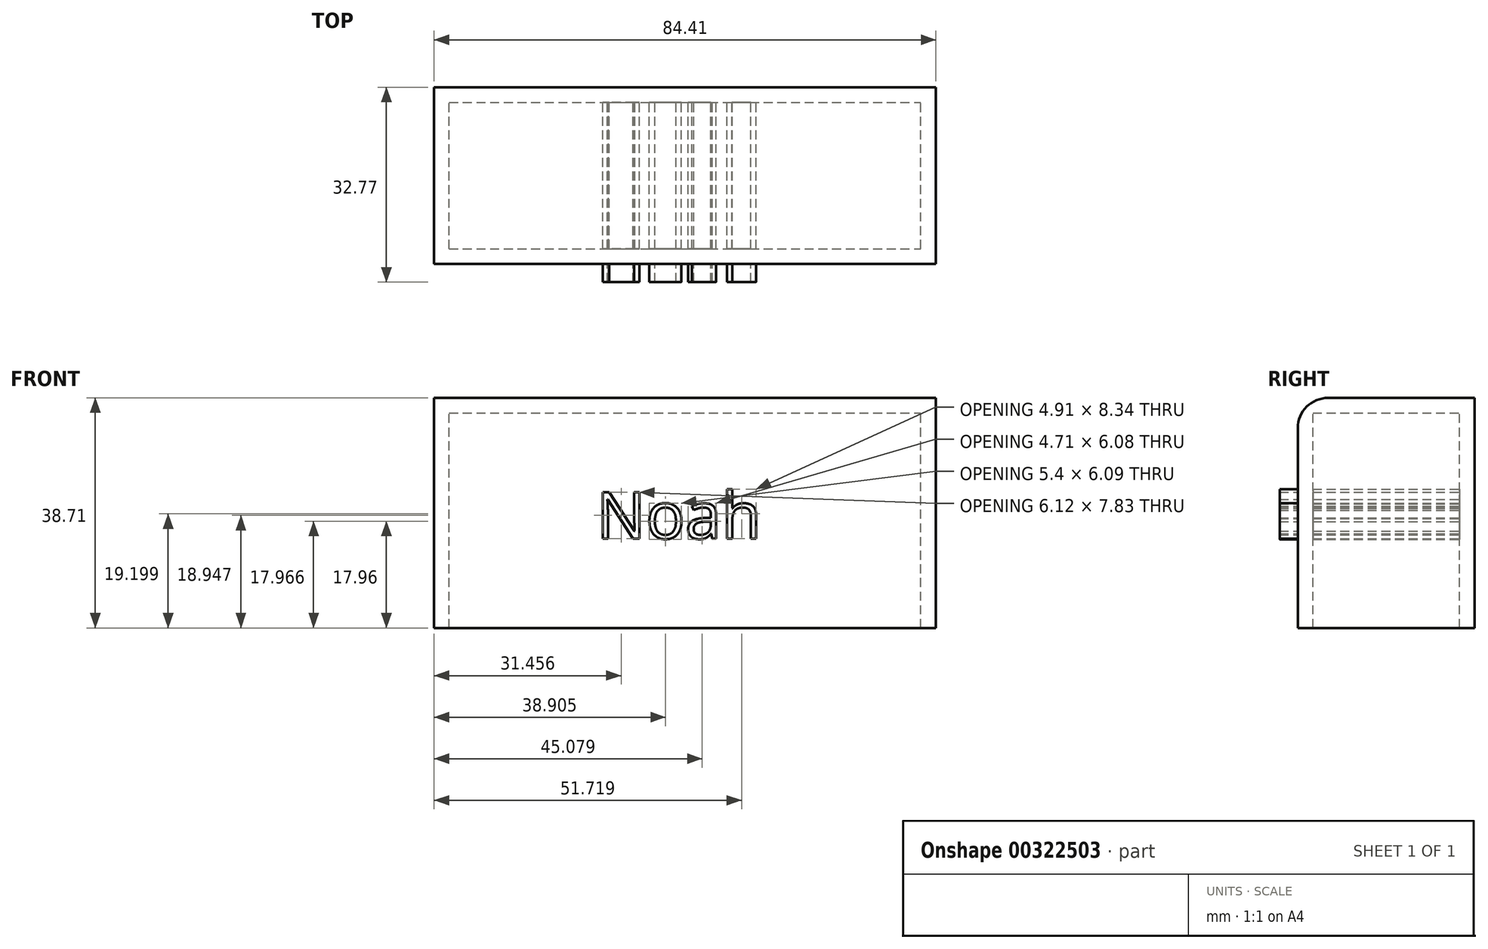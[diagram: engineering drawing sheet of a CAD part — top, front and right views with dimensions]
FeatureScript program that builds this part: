
annotation { "Feature Type Name" : "Feature", "Feature Type Description" : "" }
export const myFeature = defineFeature(function(context is Context, id is Id, definition is map)
    precondition{}
    {
        {
            var Q0;
            Q0=qCreatedBy(makeId("Front.planeOp"),FACE);
            var sketch = newSketch(context, id + "F0", { "sketchPlane" : qUnion([Q0])});
            skLineSegment(sketch, "E0.bottom", {"start": v(-40.38, 0) * mm, "end": v(44.03, 0) * mm});
            skLineSegment(sketch, "E0.top", {"start": v(-40.38, 38.71) * mm, "end": v(44.03, 38.71) * mm});
            skLineSegment(sketch, "E0.left", {"start": v(-40.38, 0) * mm, "end": v(-40.38, 38.71) * mm});
            skLineSegment(sketch, "E0.right", {"start": v(44.03, 0) * mm, "end": v(44.03, 38.71) * mm});
            skSolve(sketch);
        }
        {
            var Q0;
            Q0=makeQuery(id+"F0.imprint","IMPRINT",FACE,{"disambiguationData":[TD([[makeQuery(id+"F0.imprint","IMPRINT",EDGE,{"derivedFrom":sQuery(id+"F0.wireOp",EDGE,"E0.bottom")}),1.0]])]});
            extrude(context, id + "F1", {"entities" : qUnion([Q0]), "depth" : 29.72 * mm});
        }
        {
            var Q0;
            Q0=makeQuery(id+"F1.opExtrude","SWEPT_FACE",FACE,{"disambiguationData":[OSD([sQuery(id+"F0.wireOp",EDGE,"E0.bottom")])]});
            shell(context, id + "F2", {"entities" : qUnion([Q0]), "thickness" : 2.54 * mm});
        }
        {
            var Q0;
            Q0=makeQuery(id+"F1.opExtrude","CAP_EDGE",EDGE,{"disambiguationData":[OSD([sQuery(id+"F0.wireOp",EDGE,"E0.top")])],"isStart":false});
            fillet(context, id + "F3", {"entities" : qUnion([Q0]), "radius" : 5.08 * mm, "tangentPropagation" : true, "allowEdgeOverflow" : false});
        }
        {
            var Q0;
            Q0=qCreatedBy(makeId("Front.planeOp"),FACE);
            var sketch = newSketch(context, id + "F4", { "sketchPlane" : qUnion([Q0])});
            skText(sketch, "E1", { "text": "Noah\n", "fontName": "OpenSans-Regular.ttf"});
            const initialGuessF4  = {"E1": [-0.01306, 0.01503, 1, 0, 0.0079]};
            skSetInitialGuess(sketch, initialGuessF4);
            skSolve(sketch);
        }
        {
            var Q0;
            Q0 = qSketchRegion(id + "F4", true);
            extrude(context, id + "F5", {"entities" : qUnion([Q0]), "operationType" : NewBodyOperationType.ADD, "depth" : 32.77 * mm});
        }
    });
